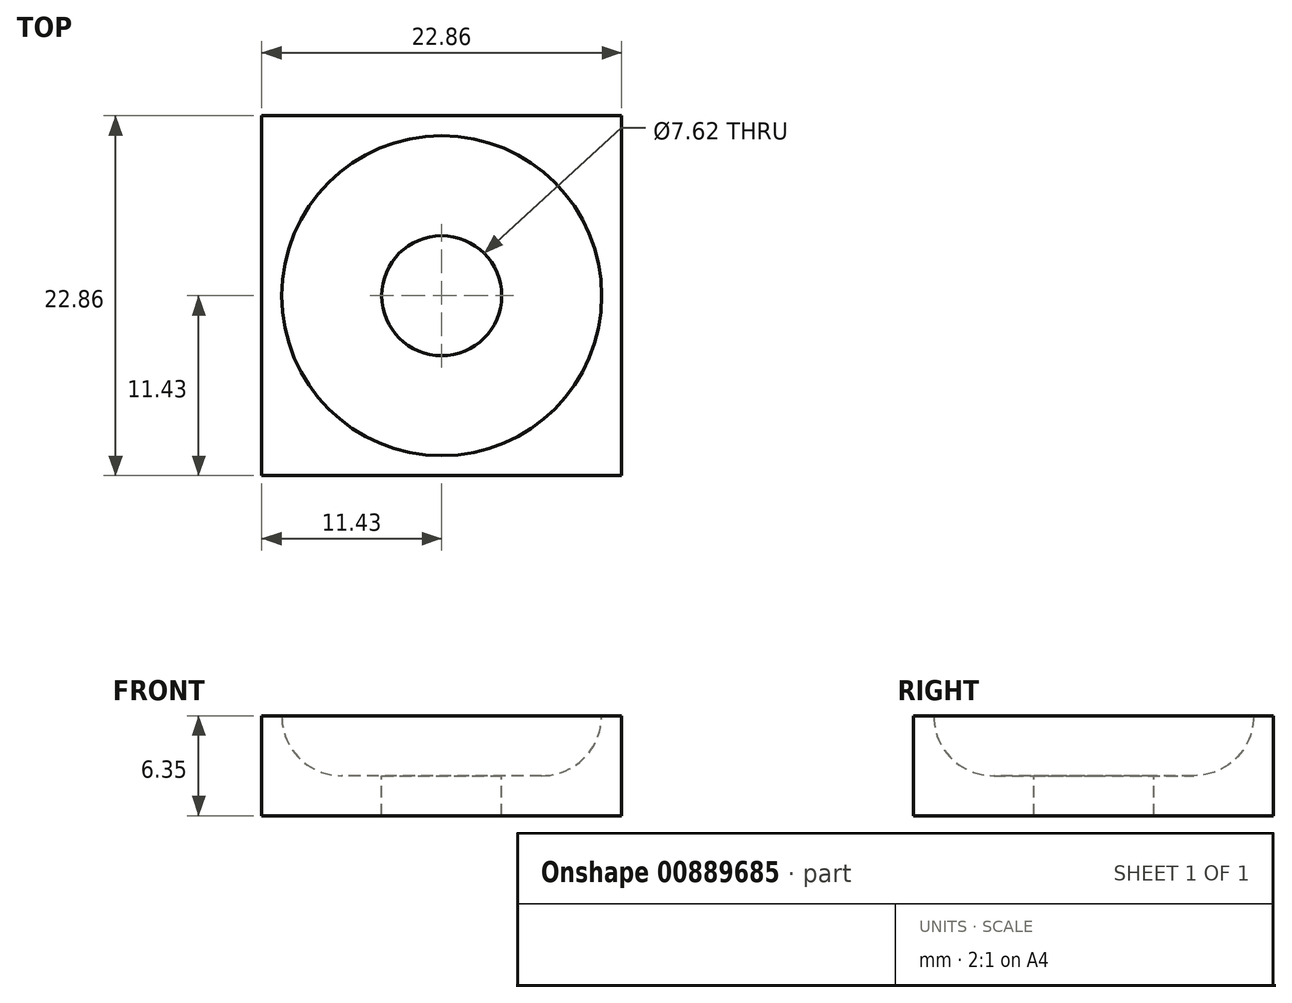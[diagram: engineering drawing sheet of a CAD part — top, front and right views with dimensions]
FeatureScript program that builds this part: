
annotation { "Feature Type Name" : "Feature", "Feature Type Description" : "" }
export const myFeature = defineFeature(function(context is Context, id is Id, definition is map)
    precondition{}
    {
        {
            var Q0;
            Q0=qCreatedBy(makeId("Top.planeOp"),FACE);
            var sketch = newSketch(context, id + "F0", { "sketchPlane" : qUnion([Q0])});
            skLineSegment(sketch, "E0.bottom", {"start": v(11.43, -11.43) * mm, "end": v(-11.43, -11.43) * mm});
            skLineSegment(sketch, "E0.top", {"start": v(11.43, 11.43) * mm, "end": v(-11.43, 11.43) * mm});
            skLineSegment(sketch, "E0.left", {"start": v(11.43, -11.43) * mm, "end": v(11.43, 11.43) * mm});
            skLineSegment(sketch, "E0.right", {"start": v(-11.43, -11.43) * mm, "end": v(-11.43, 11.43) * mm});
            skPoint(sketch, "E0.middle", {"position": v(0, 0) * mm});
            skSolve(sketch);
        }
        {
            var Q0;
            Q0=makeQuery(id+"F0.imprint","IMPRINT",FACE,{"disambiguationData":[TD([[makeQuery(id+"F0.imprint","IMPRINT",EDGE,{"derivedFrom":sQuery(id+"F0.wireOp",EDGE,"E0.bottom")}),-1.0]])]});
            extrude(context, id + "F1", {"entities" : qUnion([Q0]), "depth" : 3.8 * mm, "offsetDistance" : 25.4 * mm});
        }
        {
            var Q0;
            Q0=qCreatedBy(makeId("Front.planeOp"),FACE);
            var sketch = newSketch(context, id + "F2", { "sketchPlane" : qUnion([Q0])});
            skLineSegment(sketch, "E1", {"start": v(0, 0) * mm, "end": v(0, 3.81) * mm});
            skLineSegment(sketch, "E2", {"start": v(0, 3.81) * mm, "end": v(10.16, 3.81) * mm});
            skLineSegment(sketch, "E3", {"start": v(0, 0) * mm, "end": v(6.35, 0) * mm});
            skLineSegment(sketch, "E4", {"start": v(10.16, 3.81) * mm, "end": v(10.16, 3.81) * mm});
            skPoint(sketch, "E5.visualSharp", {"position": v(10.16, 0) * mm});
            skArc(sketch, "E5.filletArc", {"start": v(6.35, 0) * mm, "mid": v(9.04, 1.12) * mm, "end": v(10.16, 3.81) * mm});
            skSolve(sketch);
        }
        {
            var Q0;
            Q0 = qSketchRegion(id + "F2", true);
            var Q1;
            Q1=sQuery(id+"F2.wireOp",EDGE,"E1");
            revolve(context, id + "F3", {"operationType" : NewBodyOperationType.REMOVE, "surfaceOperationType" : NewSurfaceOperationType.NEW, "entities" : qUnion([Q0]), "axis" : qUnion([Q1]), "revolveType" : RevolveType.FULL, "oppositeDirection" : true});
        }
        {
            var Q0;
            Q0=makeQuery(id+"F1.opExtrude","CAP_FACE",FACE,{"disambiguationData":[OSD([sQuery(id+"F0.wireOp",EDGE,"E0.bottom"),sQuery(id+"F0.wireOp",EDGE,"E0.top"),sQuery(id+"F0.wireOp",EDGE,"E0.left"),sQuery(id+"F0.wireOp",EDGE,"E0.right")])],"isStart":true});
            var sketch = newSketch(context, id + "F4", { "sketchPlane" : qUnion([Q0])});
            skLineSegment(sketch, "E6.bottom", {"start": v(11.43, -11.43) * mm, "end": v(-11.43, -11.43) * mm});
            skLineSegment(sketch, "E6.top", {"start": v(11.43, 11.43) * mm, "end": v(-11.43, 11.43) * mm});
            skLineSegment(sketch, "E6.left", {"start": v(11.43, -11.43) * mm, "end": v(11.43, 11.43) * mm});
            skLineSegment(sketch, "E6.right", {"start": v(-11.43, -11.43) * mm, "end": v(-11.43, 11.43) * mm});
            skPoint(sketch, "E6.middle", {"position": v(0, 0) * mm});
            skCircle(sketch, "E7", {"center": v(0, 0) * mm, "radius": 3.81 * mm});
            skSolve(sketch);
        }
        {
            var Q0;
            Q0 = qSketchRegion(id + "F4", true);
            extrude(context, id + "F5", {"entities" : qUnion([Q0]), "operationType" : NewBodyOperationType.ADD, "depth" : 2.54 * mm, "offsetDistance" : 25.4 * mm});
        }
    });
